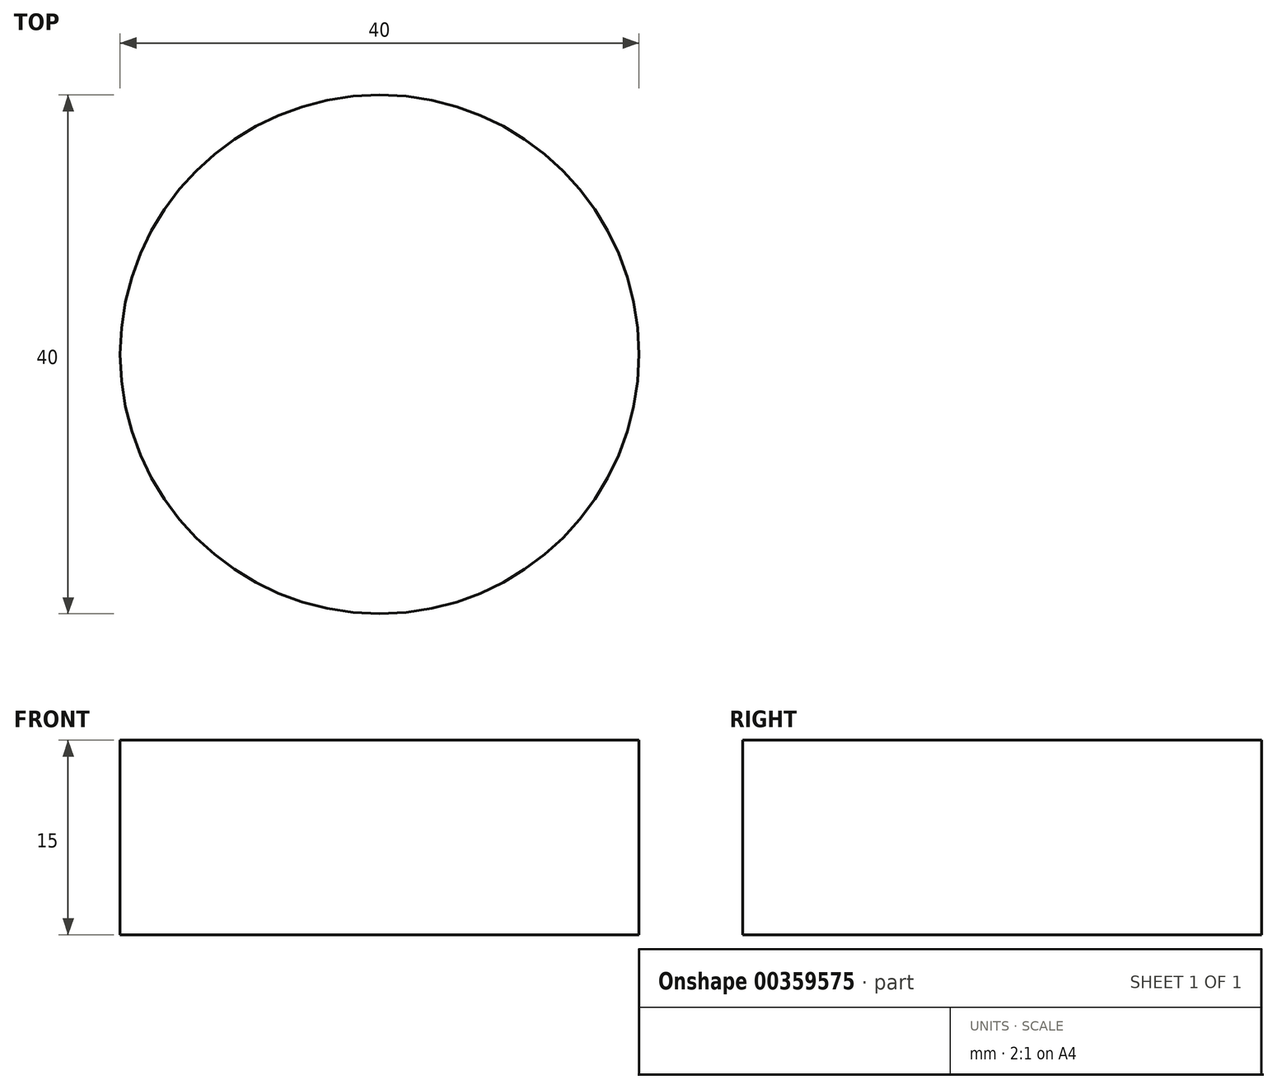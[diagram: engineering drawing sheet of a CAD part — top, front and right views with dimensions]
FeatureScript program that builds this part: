
annotation { "Feature Type Name" : "Feature", "Feature Type Description" : "" }
export const myFeature = defineFeature(function(context is Context, id is Id, definition is map)
    precondition{}
    {
        {
            var Q0;
            Q0=qCreatedBy(makeId("Top.planeOp"),FACE);
            var sketch = newSketch(context, id + "F0", { "sketchPlane" : qUnion([Q0])});
            skCircle(sketch, "E0", {"center": v(0, 0) * mm, "radius": 20 * mm});
            skCircle(sketch, "E1", {"center": v(-123.88, -30.75) * mm, "radius": 1.87 * mm});
            skSolve(sketch);
        }
        {
            var Q0;
            Q0=makeQuery(id+"F0.imprint","IMPRINT",FACE,{"disambiguationData":[TD([[makeQuery(id+"F0.imprint","IMPRINT",EDGE,{"derivedFrom":sQuery(id+"F0.wireOp",EDGE,"E0")}),1.0]])]});
            extrude(context, id + "F1", {"entities" : qUnion([Q0]), "depth" : 15 * mm});
        }
    });
